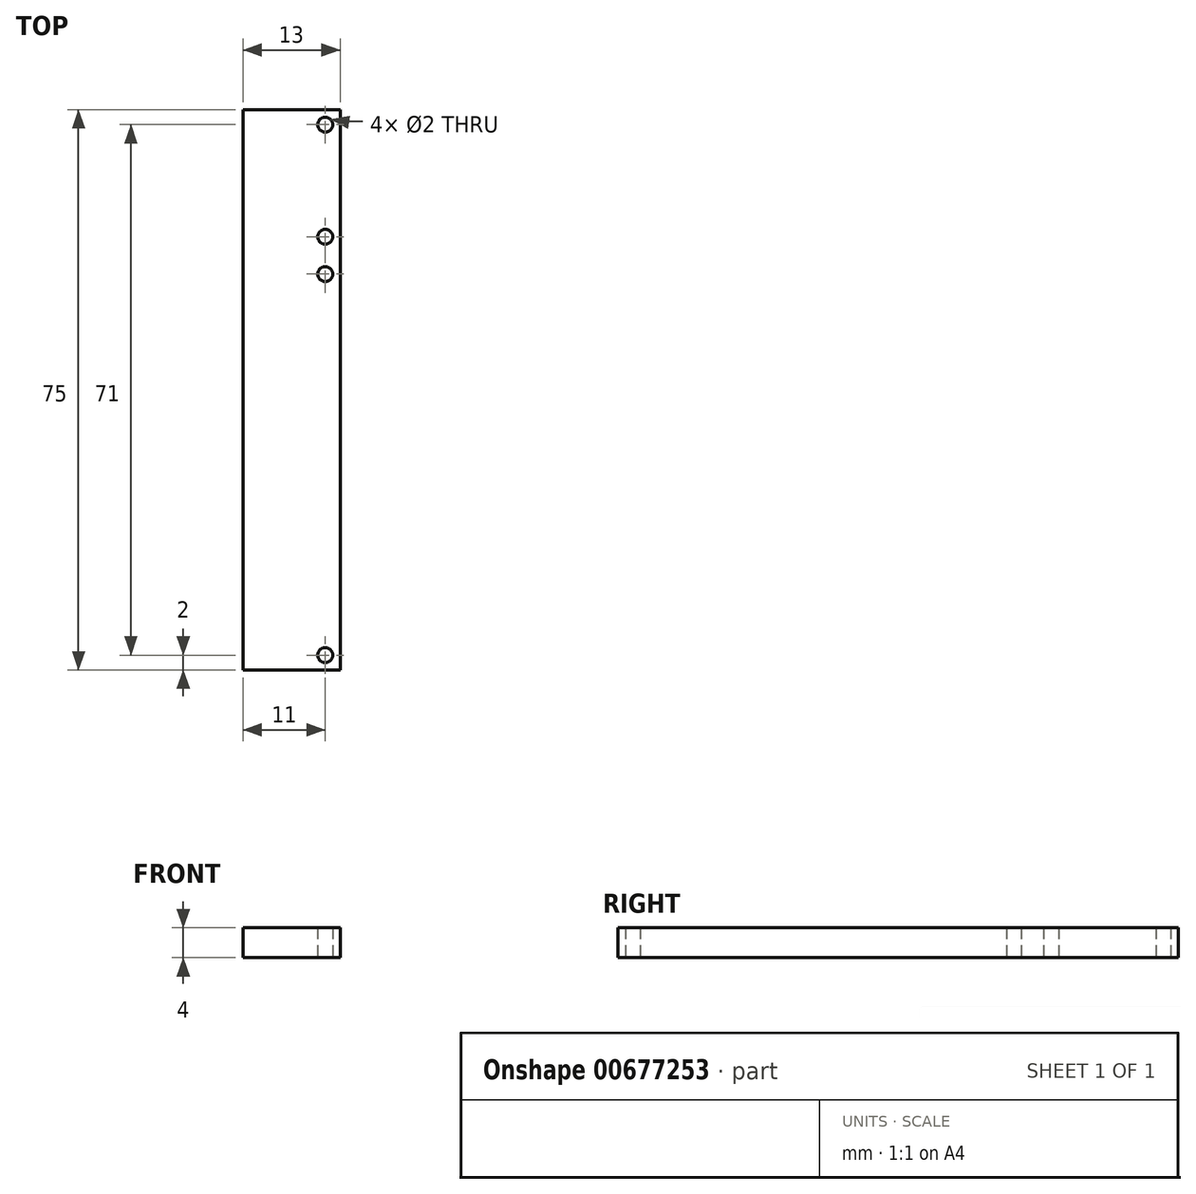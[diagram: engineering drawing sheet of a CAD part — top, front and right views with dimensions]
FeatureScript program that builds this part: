
annotation { "Feature Type Name" : "Feature", "Feature Type Description" : "" }
export const myFeature = defineFeature(function(context is Context, id is Id, definition is map)
    precondition{}
    {
        {
            var Q0;
            Q0=qCreatedBy(makeId("Top.planeOp"),FACE);
            var sketch = newSketch(context, id + "F0", { "sketchPlane" : qUnion([Q0])});
            skLineSegment(sketch, "E0.bottom", {"start": v(0, 0) * mm, "end": v(13, 0) * mm});
            skLineSegment(sketch, "E0.top", {"start": v(0, 75) * mm, "end": v(13, 75) * mm});
            skLineSegment(sketch, "E0.left", {"start": v(0, 0) * mm, "end": v(0, 75) * mm});
            skLineSegment(sketch, "E0.right", {"start": v(13, 0) * mm, "end": v(13, 75) * mm});
            skLineSegment(sketch, "E1", {"start": v(13, 0) * mm, "end": v(11, 0) * mm, "construction": true});
            skLineSegment(sketch, "E2", {"start": v(13, 0) * mm, "end": v(13, 2) * mm, "construction": true});
            skCircle(sketch, "E3", {"center": v(11, 2) * mm, "radius": 1 * mm});
            skLineSegment(sketch, "E4", {"start": v(11, 2) * mm, "end": v(11, 53) * mm, "construction": true});
            skCircle(sketch, "E5", {"center": v(11, 53) * mm, "radius": 1 * mm});
            skLineSegment(sketch, "E6", {"start": v(11, 53) * mm, "end": v(11, 58) * mm, "construction": true});
            skCircle(sketch, "E7", {"center": v(11, 58) * mm, "radius": 1 * mm});
            skLineSegment(sketch, "E8", {"start": v(11, 58) * mm, "end": v(11, 73) * mm, "construction": true});
            skCircle(sketch, "E9", {"center": v(11, 73) * mm, "radius": 1 * mm});
            skSolve(sketch);
        }
        {
            var Q0;
            Q0=makeQuery(id+"F0.imprint","IMPRINT",FACE,{"disambiguationData":[TD([[makeQuery(id+"F0.imprint","IMPRINT",EDGE,{"derivedFrom":sQuery(id+"F0.wireOp",EDGE,"E0.bottom")}),1.0]])]});
            extrude(context, id + "F1", {"entities" : qUnion([Q0]), "depth" : 4 * mm, "offsetDistance" : 25 * mm});
        }
    });
